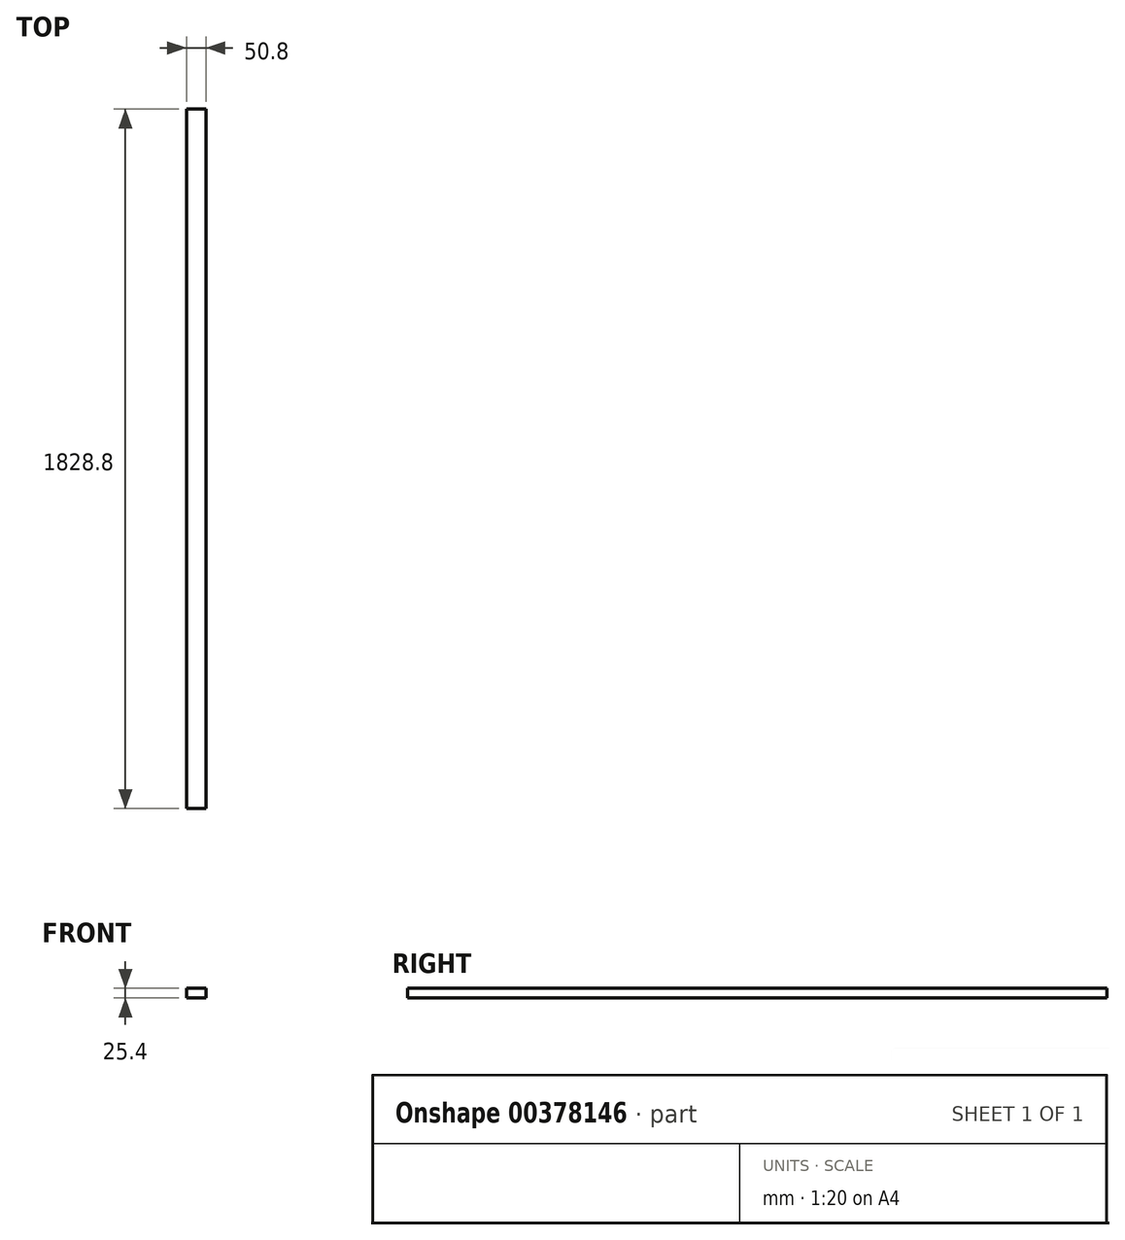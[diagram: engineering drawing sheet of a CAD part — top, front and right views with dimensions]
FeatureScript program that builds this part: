
annotation { "Feature Type Name" : "Feature", "Feature Type Description" : "" }
export const myFeature = defineFeature(function(context is Context, id is Id, definition is map)
    precondition{}
    {
        {
            var Q0;
            Q0=qCreatedBy(makeId("Front.planeOp"),FACE);
            var sketch = newSketch(context, id + "F0", { "sketchPlane" : qUnion([Q0])});
            skLineSegment(sketch, "E0.bottom", {"start": v(25.4, 12.7) * mm, "end": v(-25.4, 12.7) * mm});
            skLineSegment(sketch, "E0.top", {"start": v(25.4, -12.7) * mm, "end": v(-25.4, -12.7) * mm});
            skLineSegment(sketch, "E0.left", {"start": v(25.4, 12.7) * mm, "end": v(25.4, -12.7) * mm});
            skLineSegment(sketch, "E0.right", {"start": v(-25.4, 12.7) * mm, "end": v(-25.4, -12.7) * mm});
            skPoint(sketch, "E0.middle", {"position": v(0, 0) * mm});
            skSolve(sketch);
        }
        {
            var Q0;
            Q0 = qSketchRegion(id + "F0", true);
            extrude(context, id + "F1", {"entities" : qUnion([Q0]), "endBound" : BoundingType.SYMMETRIC, "depth" : 1828.8 * mm});
        }
    });
